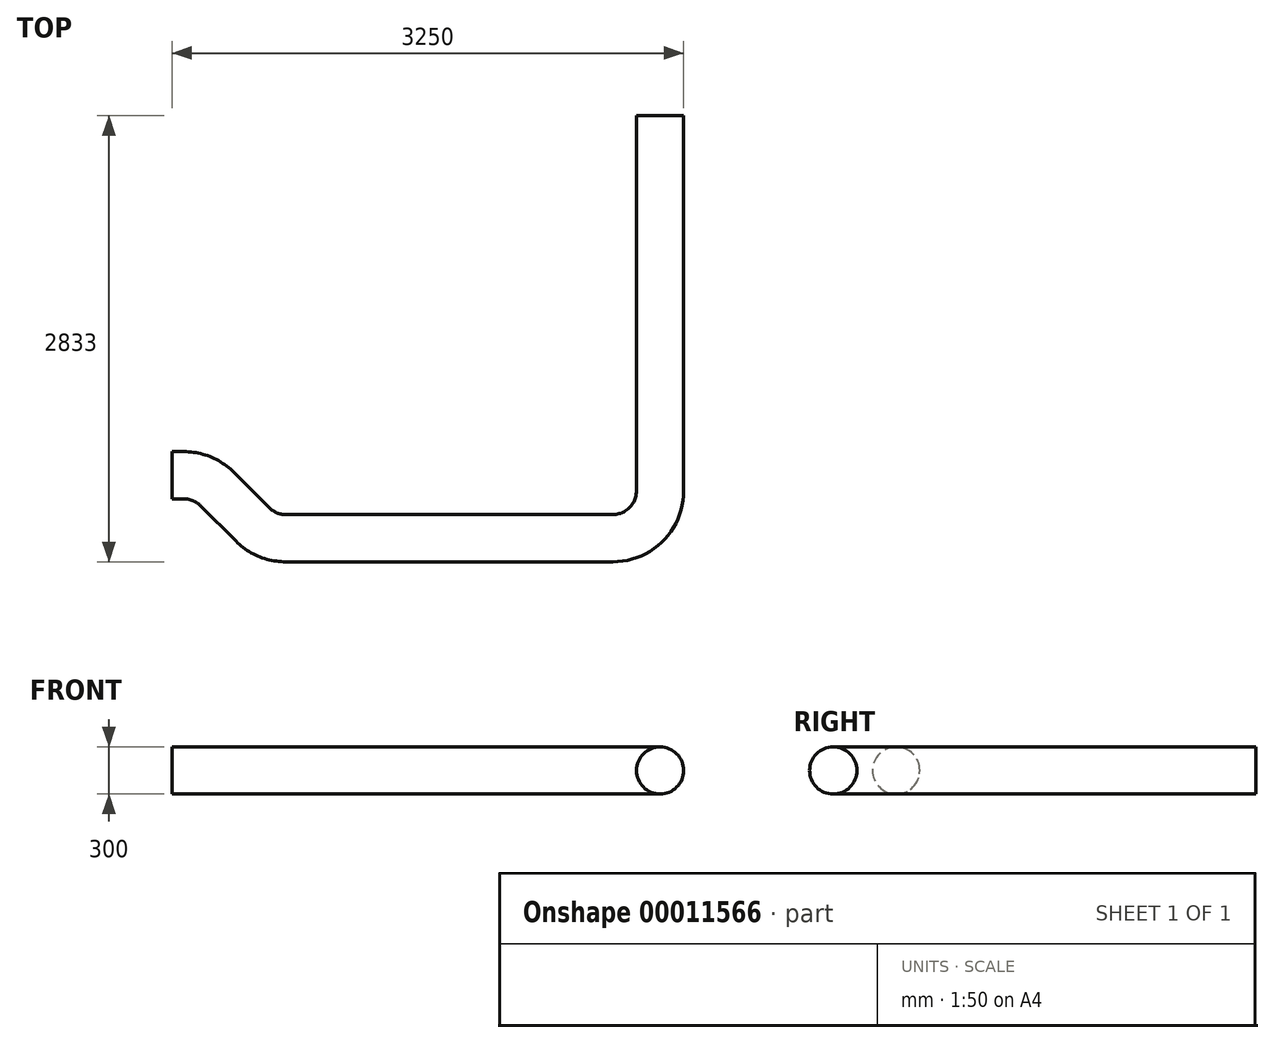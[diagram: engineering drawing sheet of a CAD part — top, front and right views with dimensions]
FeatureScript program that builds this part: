
annotation { "Feature Type Name" : "Feature", "Feature Type Description" : "" }
export const myFeature = defineFeature(function(context is Context, id is Id, definition is map)
    precondition{}
    {
        {
            var Q0;
            Q0=qCreatedBy(makeId("Top.planeOp"),FACE);
            var sketch = newSketch(context, id + "F0", { "sketchPlane" : qUnion([Q0])});
            skLineSegment(sketch, "E0", {"start": v(0, 0) * mm, "end": v(75.74, 0) * mm});
            skLineSegment(sketch, "E1", {"start": v(287.87, -87.87) * mm, "end": v(512.13, -312.13) * mm});
            skLineSegment(sketch, "E2", {"start": v(724.26, -400) * mm, "end": v(2800, -400) * mm});
            skLineSegment(sketch, "E3", {"start": v(3100, -100) * mm, "end": v(3100, 2283) * mm});
            skPoint(sketch, "E4.visualSharp", {"position": v(200, 0) * mm});
            skArc(sketch, "E4.filletArc", {"start": v(287.87, -87.87) * mm, "mid": v(190.54, -22.84) * mm, "end": v(75.74, 0) * mm});
            skPoint(sketch, "E5.visualSharp", {"position": v(600, -400) * mm});
            skArc(sketch, "E5.filletArc", {"start": v(512.13, -312.13) * mm, "mid": v(609.46, -377.16) * mm, "end": v(724.26, -400) * mm});
            skPoint(sketch, "E6.visualSharp", {"position": v(3100, -400) * mm});
            skArc(sketch, "E6.filletArc", {"start": v(2800, -400) * mm, "mid": v(3012.13, -312.13) * mm, "end": v(3100, -100) * mm});
            skSolve(sketch);
        }
        {
            var Q0;
            Q0=qCreatedBy(makeId("Right.planeOp"),FACE);
            var sketch = newSketch(context, id + "F1", { "sketchPlane" : qUnion([Q0])});
            skCircle(sketch, "E7", {"center": v(0, 0) * mm, "radius": 150 * mm});
            skSolve(sketch);
        }
        {
            var Q0;
            Q0 = qSketchRegion(id + "F1", true);
            var Q1;
            Q1 = qBodyType(qCreatedBy(id + "F0" ,EDGE), BodyType.WIRE);
            sweep(context, id + "F2", {"profiles" : qUnion([Q0]), "path" : qUnion([Q1])});
        }
    });
